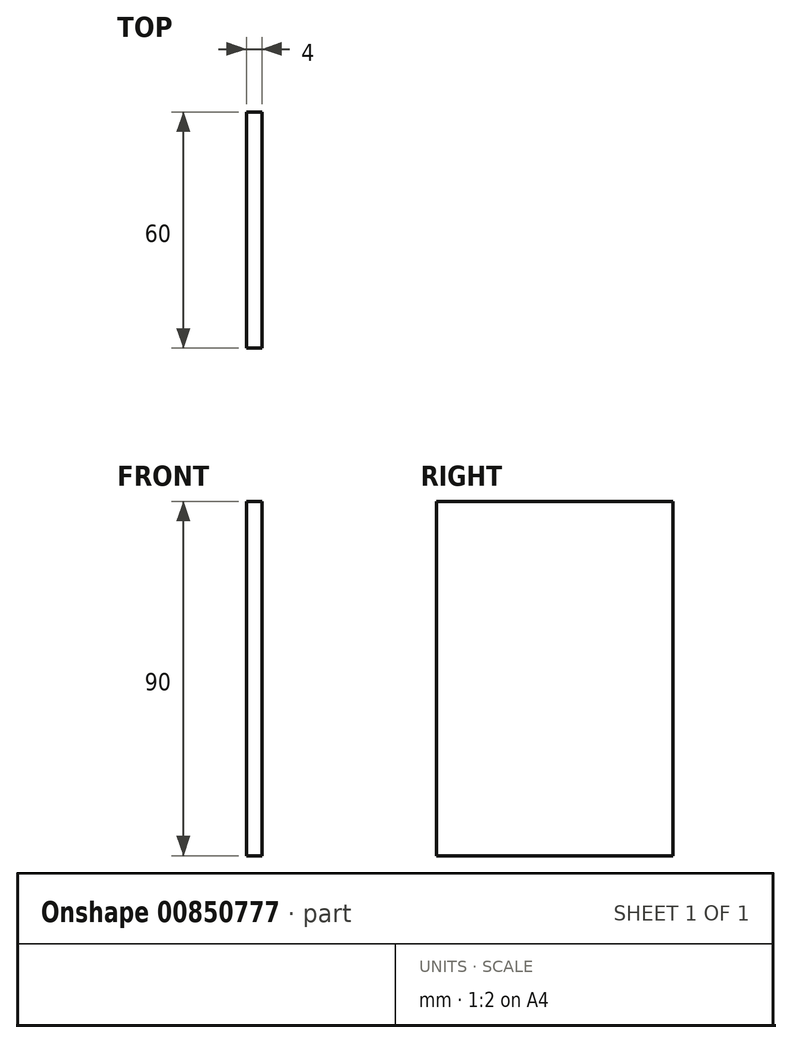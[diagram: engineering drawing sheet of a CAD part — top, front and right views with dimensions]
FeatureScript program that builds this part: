
annotation { "Feature Type Name" : "Feature", "Feature Type Description" : "" }
export const myFeature = defineFeature(function(context is Context, id is Id, definition is map)
    precondition{}
    {
        {
            var Q0;
            Q0=qCreatedBy(makeId("Right.planeOp"),FACE);
            var sketch = newSketch(context, id + "F0", { "sketchPlane" : qUnion([Q0])});
            skLineSegment(sketch, "E0.bottom", {"start": v(-30, 45) * mm, "end": v(30, 45) * mm});
            skLineSegment(sketch, "E0.top", {"start": v(-30, -45) * mm, "end": v(30, -45) * mm});
            skLineSegment(sketch, "E0.left", {"start": v(-30, 45) * mm, "end": v(-30, -45) * mm});
            skLineSegment(sketch, "E0.right", {"start": v(30, 45) * mm, "end": v(30, -45) * mm});
            skPoint(sketch, "E0.middle", {"position": v(0, 0) * mm});
            skSolve(sketch);
        }
        {
            var Q0;
            Q0 = qSketchRegion(id + "F0", true);
            extrude(context, id + "F1", {"entities" : qUnion([Q0]), "depth" : 4 * mm, "offsetDistance" : 25 * mm});
        }
    });
